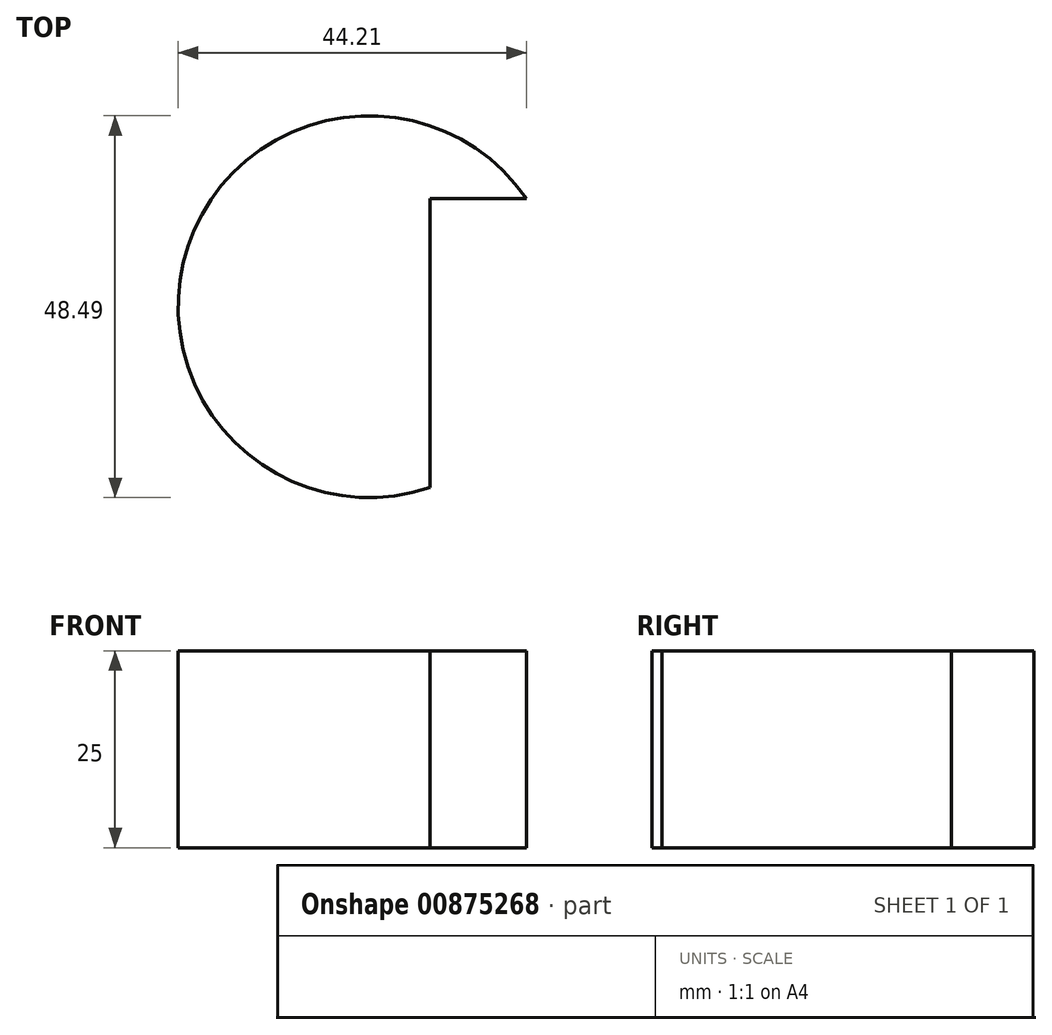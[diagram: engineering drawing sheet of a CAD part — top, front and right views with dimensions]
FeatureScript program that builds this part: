
annotation { "Feature Type Name" : "Feature", "Feature Type Description" : "" }
export const myFeature = defineFeature(function(context is Context, id is Id, definition is map)
    precondition{}
    {
        {
            var Q0;
            Q0=qCreatedBy(makeId("Top.planeOp"),FACE);
            var sketch = newSketch(context, id + "F0", { "sketchPlane" : qUnion([Q0])});
            skCircle(sketch, "E0", {"center": v(-42.33, 22.43) * mm, "radius": 24.24 * mm});
            skLineSegment(sketch, "E1.bottom", {"start": v(12.66, 36.18) * mm, "end": v(-34.61, 36.18) * mm});
            skLineSegment(sketch, "E1.top", {"start": v(12.66, -15.2) * mm, "end": v(-34.61, -15.2) * mm});
            skLineSegment(sketch, "E1.left", {"start": v(12.66, 36.18) * mm, "end": v(12.66, -15.2) * mm});
            skLineSegment(sketch, "E1.right", {"start": v(-34.61, 36.18) * mm, "end": v(-34.61, -15.2) * mm});
            skSolve(sketch);
        }
        {
            var Q0;
            {var subQ0=sQuery(id+"F0.wireOp",EDGE,"E1.bottom");var subQ1=sQuery(id+"F0.wireOp",EDGE,"E0");var subQ2=makeQuery(id+"F0.imprint","INTERSECT",VERTEX,{"derivedFrom":[subQ1,subQ0]});Q0=makeQuery(id+"F0.imprint","IMPRINT",FACE,{"disambiguationData":[TD([[makeQuery(id+"F0.imprint","IMPRINT",EDGE,{"disambiguationData":[TD([[subQ2,-1.0]])],"derivedFrom":subQ1}),1.0]])]});}
            extrude(context, id + "F1", {"entities" : qUnion([Q0]), "depth" : 25 * mm, "offsetDistance" : 25 * mm});
        }
    });
